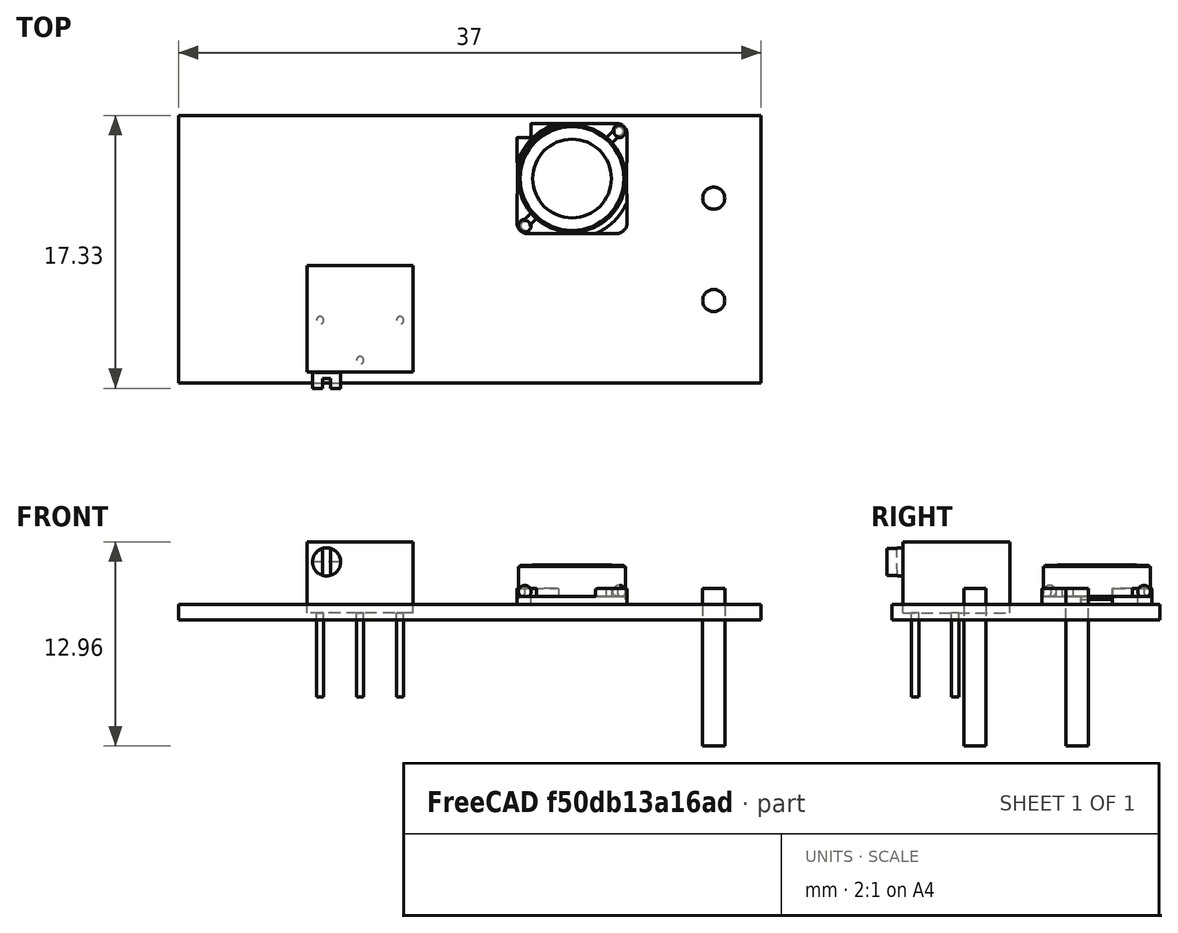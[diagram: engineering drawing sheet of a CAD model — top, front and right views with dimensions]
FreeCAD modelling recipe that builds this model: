
FCSTD DOCUMENT  (FreeCAD 0.16R)
Label: elevador
License: All rights reserved
LicenseURL: http://en.wikipedia.org/wiki/All_rights_reserved
objects: Part::Mirroring×3, Part::Feature×2, Part::Box×1, Part::Cylinder×1
note: 7 computed .brp shape members not serialized (recipe doc carries the construction recipe); baked Part::Feature solids carry a one-line shape summary decoded from their .brp

FEATURE [Part::Box] Box  label="Cubo"
  Height = 1
  Length = 37
  Width = 17
FEATURE [Part::Cylinder] Cylinder  label="Cilindro"
  Angle = 360
  Height = 10
  Placement = pos=(3,5.25,-8) rot=(0,0,1;0rad)
  Radius = 0.7
FEATURE [Part::Mirroring] Part__Mirroring  label="Cilindro (Mirror #1)"
  Base = (0,0,0)
  Normal = (0,0,1)
  Placement = pos=(0,6.5,-6) rot=(0,0,1;0rad)
  Source = -> Cylinder
FEATURE [Part::Mirroring] Part__Mirroring001  label="Cilindro (Mirror #2)"
  Base = (0,0,0)
  Normal = (0,0,1)
  Placement = pos=(31,0,-6) rot=(0,0,1;0rad)
  Source = -> Part__Mirroring
FEATURE [Part::Mirroring] Part__Mirroring002  label="Cilindro (Mirror #3)"
  Base = (0,0,0)
  Normal = (0,0,1)
  Placement = pos=(31,0,-6) rot=(0,0,1;0rad)
  Source = -> Cylinder
FEATURE [Part::Feature] Part__Feature  label="Sfär_fd_sp"
  Placement = pos=(25,13,1) rot=(0,0,1;0rad)
  shape: bbox 7.058 x 7.058 x 2.5 mm, 79 faces (baked)
FEATURE [Part::Feature] Part__Feature001  label="Potentiometer_Bourns_3266P_Horizontal"
  Placement = pos=(9,4,0) rot=(0,0,1;1.5708rad)
  shape: bbox 6.71 x 7.808 x 9.84 mm, 19 faces (baked)
